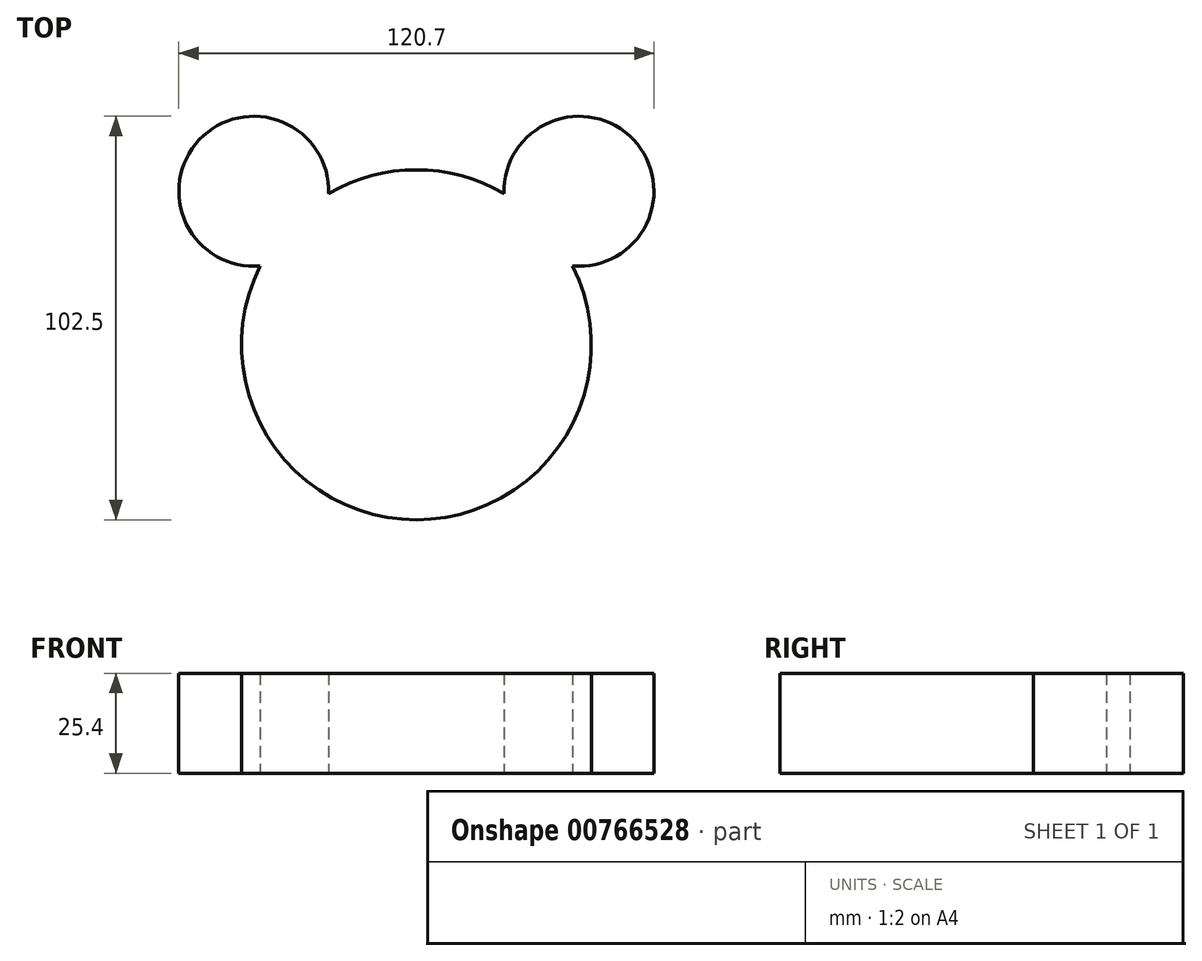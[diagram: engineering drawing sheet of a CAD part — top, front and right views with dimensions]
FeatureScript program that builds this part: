
annotation { "Feature Type Name" : "Feature", "Feature Type Description" : "" }
export const myFeature = defineFeature(function(context is Context, id is Id, definition is map)
    precondition{}
    {
        {
            var Q0;
            Q0=qCreatedBy(makeId("Top.planeOp"),FACE);
            var sketch = newSketch(context, id + "F0", { "sketchPlane" : qUnion([Q0])});
            skCircle(sketch, "E0", {"center": v(0, 0) * mm, "radius": 44.45 * mm});
            skCircle(sketch, "E1", {"center": v(41.3, 39) * mm, "radius": 19.05 * mm});
            skCircle(sketch, "E2.MirrorC", {"center": v(-41.3, 39) * mm, "radius": 19.05 * mm});
            skSolve(sketch);
        }
        {
            var Q0;
            {var subQ0=sQuery(id+"F0.wireOp",EDGE,"E1");var subQ1=sQuery(id+"F0.wireOp",EDGE,"E0");var subQ2=makeQuery(id+"F0.imprint","INTERSECT",VERTEX,{"disambiguationData":[OD(0.0)],"derivedFrom":[subQ1,subQ0]});Q0=makeQuery(id+"F0.imprint","IMPRINT",FACE,{"disambiguationData":[TD([[makeQuery(id+"F0.imprint","IMPRINT",EDGE,{"disambiguationData":[TD([[subQ2,-1.0]])],"derivedFrom":subQ1}),1.0]])]});}
            var Q1;
            {var subQ0=sQuery(id+"F0.wireOp",EDGE,"E2.MirrorC");var subQ1=sQuery(id+"F0.wireOp",EDGE,"E0");var subQ2=makeQuery(id+"F0.imprint","INTERSECT",VERTEX,{"disambiguationData":[OD(0.0)],"derivedFrom":[subQ1,subQ0]});Q1=makeQuery(id+"F0.imprint","IMPRINT",FACE,{"disambiguationData":[TD([[makeQuery(id+"F0.imprint","IMPRINT",EDGE,{"disambiguationData":[TD([[subQ2,-1.0]])],"derivedFrom":subQ1}),1.0]])]});}
            var Q2;
            {var subQ0=sQuery(id+"F0.wireOp",EDGE,"E2.MirrorC");var subQ1=sQuery(id+"F0.wireOp",EDGE,"E0");var subQ2=makeQuery(id+"F0.imprint","INTERSECT",VERTEX,{"disambiguationData":[OD(0.0)],"derivedFrom":[subQ1,subQ0]});Q2=makeQuery(id+"F0.imprint","IMPRINT",FACE,{"disambiguationData":[TD([[makeQuery(id+"F0.imprint","IMPRINT",EDGE,{"disambiguationData":[TD([[subQ2,-1.0]])],"derivedFrom":subQ1}),-1.0]])]});}
            var Q3;
            {var subQ0=sQuery(id+"F0.wireOp",EDGE,"E1");var subQ1=sQuery(id+"F0.wireOp",EDGE,"E0");var subQ2=makeQuery(id+"F0.imprint","INTERSECT",VERTEX,{"disambiguationData":[OD(0.0)],"derivedFrom":[subQ1,subQ0]});Q3=makeQuery(id+"F0.imprint","IMPRINT",FACE,{"disambiguationData":[TD([[makeQuery(id+"F0.imprint","IMPRINT",EDGE,{"disambiguationData":[TD([[subQ2,1.0]])],"derivedFrom":subQ1}),-1.0]])]});}
            var Q4;
            {var subQ0=sQuery(id+"F0.wireOp",EDGE,"E1");var subQ1=sQuery(id+"F0.wireOp",EDGE,"E0");var subQ2=makeQuery(id+"F0.imprint","INTERSECT",VERTEX,{"disambiguationData":[OD(0.0)],"derivedFrom":[subQ1,subQ0]});Q4=makeQuery(id+"F0.imprint","IMPRINT",FACE,{"disambiguationData":[TD([[makeQuery(id+"F0.imprint","IMPRINT",EDGE,{"disambiguationData":[TD([[subQ2,1.0]])],"derivedFrom":subQ1}),1.0]])]});}
            extrude(context, id + "F1", {"entities" : qUnion([Q0, Q1, Q2, Q3, Q4]), "depth" : 25.4 * mm, "offsetDistance" : 25.4 * mm});
        }
    });
